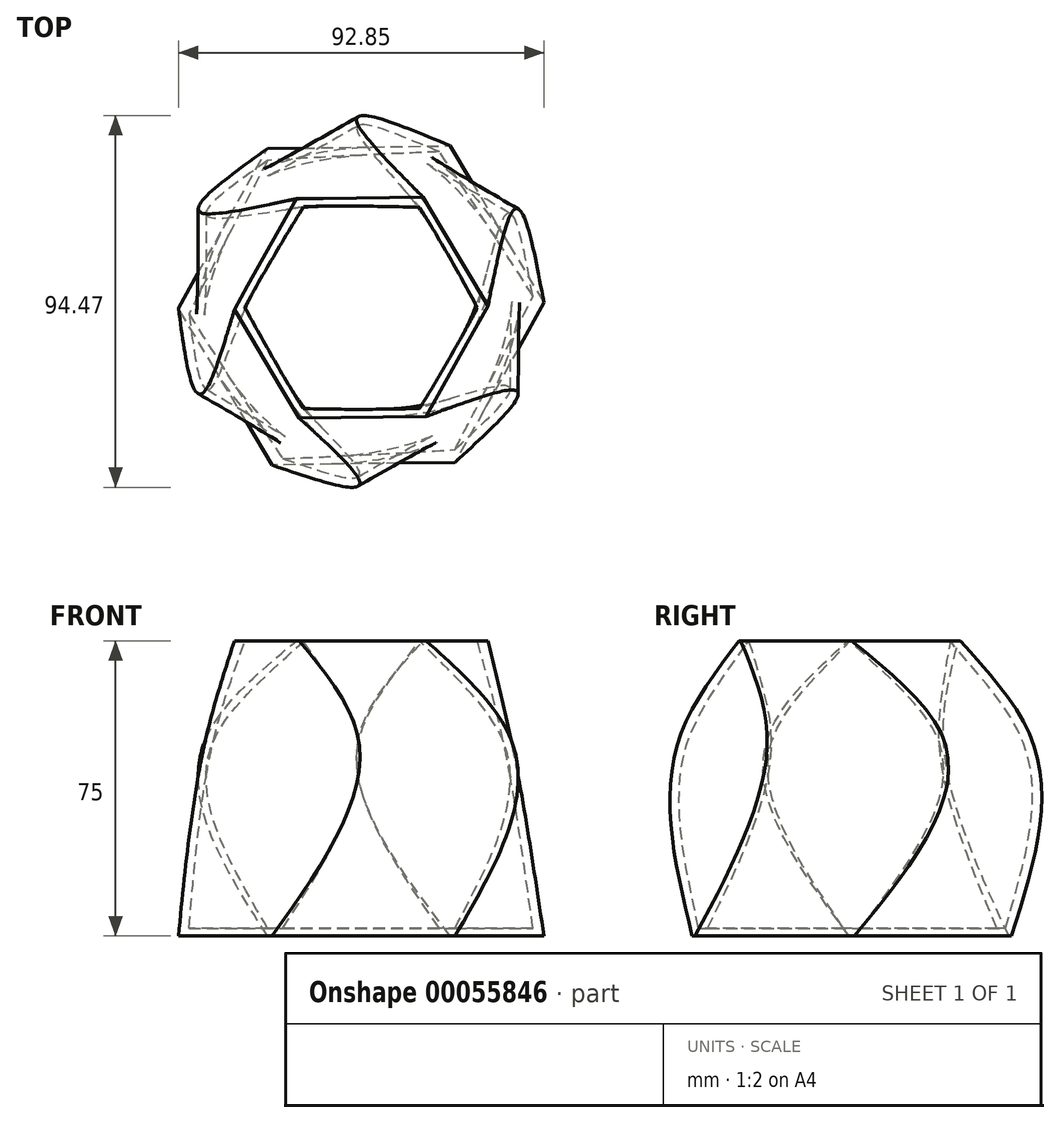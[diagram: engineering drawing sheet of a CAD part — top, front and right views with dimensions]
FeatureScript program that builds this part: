
annotation { "Feature Type Name" : "Feature", "Feature Type Description" : "" }
export const myFeature = defineFeature(function(context is Context, id is Id, definition is map)
    precondition{}
    {
        {
            var Q0;
            Q0=qCreatedBy(makeId("Top.planeOp"),FACE);
            var sketch = newSketch(context, id + "F0", { "sketchPlane" : qUnion([Q0])});
            skCircle(sketch, "E0.cCircle", {"center": v(-2.74, 5.03) * mm, "radius": 40.2 * mm, "construction": true});
            skLineSegment(sketch, "E0.0", {"start": v(43.68, 5.73) * mm, "end": v(21.08, -34.82) * mm});
            skLineSegment(sketch, "E0.1", {"start": v(21.08, -34.82) * mm, "end": v(-25.35, -35.52) * mm});
            skLineSegment(sketch, "E0.2", {"start": v(-25.35, -35.52) * mm, "end": v(-49.17, 4.33) * mm});
            skLineSegment(sketch, "E0.3", {"start": v(-49.17, 4.33) * mm, "end": v(-26.57, 44.88) * mm});
            skLineSegment(sketch, "E0.4", {"start": v(-26.57, 44.88) * mm, "end": v(19.86, 45.59) * mm});
            skLineSegment(sketch, "E0.5", {"start": v(19.86, 45.59) * mm, "end": v(43.68, 5.73) * mm});
            skPoint(sketch, "E0.0.midPoint", {"position": v(32.38, -14.54) * mm});
            skSolve(sketch);
        }
        {
            var Q0;
            Q0=qCreatedBy(makeId("Top.planeOp"),FACE);
            cPlane(context, id + "F1", {"entities" : qUnion([Q0]), "cplaneType" : CPlaneType.OFFSET, "offset" : 50 * mm, "width" : 150 * mm, "height" : 150 * mm});
        }
        {
            var Q0;
            Q0=qCreatedBy(id+"F1.planeOp",FACE);
            cPlane(context, id + "F2", {"entities" : qUnion([Q0]), "cplaneType" : CPlaneType.OFFSET, "offset" : 25 * mm, "width" : 150 * mm, "height" : 150 * mm});
        }
        {
            var Q0;
            Q0=qCreatedBy(id+"F1.planeOp",FACE);
            var sketch = newSketch(context, id + "F3", { "sketchPlane" : qUnion([Q0])});
            skCircle(sketch, "E1.cCircle", {"center": v(-3.48, 5.95) * mm, "radius": 38.78 * mm, "construction": true});
            skLineSegment(sketch, "E1.0", {"start": v(35.3, 28.34) * mm, "end": v(35.3, -16.44) * mm});
            skLineSegment(sketch, "E1.1", {"start": v(35.3, -16.44) * mm, "end": v(-3.48, -38.83) * mm});
            skLineSegment(sketch, "E1.2", {"start": v(-3.48, -38.83) * mm, "end": v(-42.26, -16.44) * mm});
            skLineSegment(sketch, "E1.3", {"start": v(-42.26, -16.44) * mm, "end": v(-42.26, 28.34) * mm});
            skLineSegment(sketch, "E1.4", {"start": v(-42.26, 28.34) * mm, "end": v(-3.48, 50.72) * mm});
            skLineSegment(sketch, "E1.5", {"start": v(-3.48, 50.72) * mm, "end": v(35.3, 28.34) * mm});
            skPoint(sketch, "E1.0.midPoint", {"position": v(35.3, 5.95) * mm});
            skSolve(sketch);
        }
        {
            var Q0;
            Q0=qCreatedBy(id+"F2.planeOp",FACE);
            var sketch = newSketch(context, id + "F4", { "sketchPlane" : qUnion([Q0])});
            skCircle(sketch, "E2.cCircle", {"center": v(-2.74, 4.48) * mm, "radius": 27.89 * mm, "construction": true});
            skLineSegment(sketch, "E2.0", {"start": v(12.98, 32.59) * mm, "end": v(29.46, 4.91) * mm});
            skLineSegment(sketch, "E2.1", {"start": v(29.46, 4.91) * mm, "end": v(13.73, -23.19) * mm});
            skLineSegment(sketch, "E2.2", {"start": v(13.73, -23.19) * mm, "end": v(-18.47, -23.62) * mm});
            skLineSegment(sketch, "E2.3", {"start": v(-18.47, -23.62) * mm, "end": v(-34.95, 4.05) * mm});
            skLineSegment(sketch, "E2.4", {"start": v(-34.95, 4.05) * mm, "end": v(-19.22, 32.15) * mm});
            skLineSegment(sketch, "E2.5", {"start": v(-19.22, 32.15) * mm, "end": v(12.98, 32.59) * mm});
            skPoint(sketch, "E2.0.midPoint", {"position": v(21.22, 18.75) * mm});
            skSolve(sketch);
        }
        {
            var Q0;
            Q0=makeQuery(id+"F0.imprint","IMPRINT",FACE,{"disambiguationData":[TD([[makeQuery(id+"F0.imprint","IMPRINT",EDGE,{"derivedFrom":sQuery(id+"F0.wireOp",EDGE,"E0.0")}),-1.0]])]});
            var Q1;
            Q1=makeQuery(id+"F3.imprint","IMPRINT",FACE,{"disambiguationData":[TD([[makeQuery(id+"F3.imprint","IMPRINT",EDGE,{"derivedFrom":sQuery(id+"F3.wireOp",EDGE,"E1.0")}),-1.0]])]});
            var Q2;
            Q2=makeQuery(id+"F4.imprint","IMPRINT",FACE,{"disambiguationData":[TD([[makeQuery(id+"F4.imprint","IMPRINT",EDGE,{"derivedFrom":sQuery(id+"F4.wireOp",EDGE,"E2.0")}),-1.0]])]});
            loft(context, id + "F5", {"sheetProfilesArray" : [{ "sheetProfileEntities" : qUnion([Q0]) }, { "sheetProfileEntities" : qUnion([Q1]) }, { "sheetProfileEntities" : qUnion([Q2]) }]});
        }
        {
            var Q0;
            Q0=makeQuery(id+"F5.opLoft","CAP_FACE",FACE,{"disambiguationData":[OSD([makeQuery(id+"F4.imprint","IMPRINT",FACE,{"disambiguationData":[TD([[makeQuery(id+"F4.imprint","IMPRINT",EDGE,{"derivedFrom":sQuery(id+"F4.wireOp",EDGE,"E2.0")}),-1.0]])]})])],"isStart":true});
            shell(context, id + "F6", {"entities" : qUnion([Q0]), "thickness" : 2 * mm});
        }
    });
